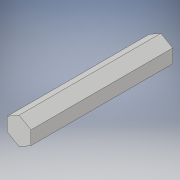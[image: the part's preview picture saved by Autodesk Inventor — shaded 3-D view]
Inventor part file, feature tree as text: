
AUTODESK INVENTOR PART (.ipt)
format: ipt  version: 2018 (Build 220112000, 112)  size: 92,160 bytes
history: native  units: in
note: dims shown in document units (in); Inventor stores cm internally (conversion verified against a paired STEP export)
features: extrude x1, sketch x1
ambient origin geometry x8: Origin, YZ Plane, XZ Plane, XY Plane, X Axis, Y Axis, Z Axis, Center Point
bodies: Solid1 (feature_tree)
feature tree (2):
  extrude  "Extrusion1"  Depth=3.0in TaperAngle=0.0deg
  sketch  "Sketch1"  dims[d0=0.5in d1=3.0in d2=0.0in]
